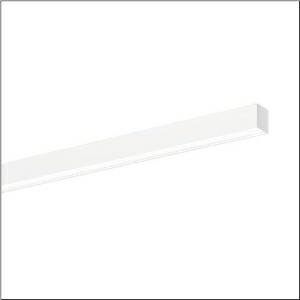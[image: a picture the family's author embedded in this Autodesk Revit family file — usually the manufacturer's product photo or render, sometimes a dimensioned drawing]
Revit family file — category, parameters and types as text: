
# Revit family: silica_r__21_51mx20db32wb_39d1
name_source: partatom
category: Lighting Fixtures
units: mm (PartAtom-declared; Revit-internal decimal feet)

## family parameters
Cut with Voids When Loaded = No
Host = Face
Light Source = No
Part Type = Normal
Room Calculation Point = No
Round Connector Dimension = Use Diameter
Shared = No

## types (1)
- --- (1 x LED, 3000 lm, 20.2 W, 3000K)
    Apparent Load = 20 VA
    CIE Flux Codes = 48 79 96 100 100
    Color Rendering = 80
    Color Temperature = 3000K
    Default Elevation = 1800 mm
    Description = Silica® 21, office luminaire, primary optical cover: cover, of PMMA, opal, light emission: direct distribution, primary light characteristic: symmetric, installation type: surface-mounted, LED, rated luminous flux: 3.000lm, luminous efficacy: 149lm/W, light colour: 830, colour temperature: 3000K, control gear: DALI 2, with terminal, 3+2-pole, max. 2.5mm², mains connection: 220..240V, AC, 50/60Hz, luminaire housing, of aluminium, traffic white (RAL 9016), length: 1.504mm, width: 53mm, height: 53mm, protection rating (complete): IP20, insulation class (complete): insulation class I (protective earthing), certification: CE, permissible operating ambient temperature: 0..+35°C, standard: EN 50419, packaging unit: 1 piece
    Height = 53 mm
    Lamp = 1 x LED
    Lamp Light Flux = 3000 lm
    Lamp Power = 20.2 W
    Lamp count = 1
    Length = 1504 mm
    Luminous efficacy = 149 lm/W
    Manufacturer = Siteco
    ModVariant = No
    Model = 51MX20DB32WB
    Mounting Place = Ceiling
    Mounting Type = Surface mounted
    Number of Poles = 1
    OnlyDefault = Yes
    Power Factor = 1
    Product Name = Silica® 21
    Product group = office luminaire | ceiling mounted
    ProductGroupID = 302
    Protection Class = Protection class I
    Protection Degree = IP 20
    RLX_Detail_Level = 1
    RLX_Emergency_Light_Flux = 0 lm
    RLX_Emergency_Type = 0
    RLX_Emergency_Type_DB = No
    RlxData = <blob elided: 23629 chars, md5=d0eb1477>
    Socket = socket
    Standby Power = 0 W
    System Light Flux = 3000 lm
    System Power = 20 W
    Type Comments = factory setting: luminous flux: 100 % | dim-lin: 254 | 233 mA
    Type Image = l_1335877.jpg
    URL = http://relux.com
    VarID = @adj_118130
    Voltage = 0 V
    Weight = 0.00 kg
    Width = 53 mm

## geometry (parser evidence)
native form markers: Blend x4, Sweep x11
no freeform markers — native parametric forms only
